annotation { "Feature Type Name" : "Feature", "Feature Type Description" : "" }
export const myFeature = defineFeature(function(context is Context, id is Id, definition is map)
    precondition{}
    {
        {
            var Q0;
            Q0=qCreatedBy(makeId("Right.planeOp"),FACE);
            var sketch = newSketch(context, id + "F0", { "sketchPlane" : qUnion([Q0])});
            skLineSegment(sketch, "E0", {"start": v(-15.9, -11.43) * mm, "end": v(-15.9, -19.05) * mm});
            skLineSegment(sketch, "E1", {"start": v(-15.9, -19.05) * mm, "end": v(-23.53, -19.05) * mm});
            skLineSegment(sketch, "E2", {"start": v(-23.53, 25.4) * mm, "end": v(-15.9, 25.4) * mm});
            skLineSegment(sketch, "E3", {"start": v(-15.9, 25.4) * mm, "end": v(0, 0) * mm});
            skLineSegment(sketch, "E4", {"start": v(0, 0) * mm, "end": v(0, 25.4) * mm});
            skLineSegment(sketch, "E5", {"start": v(0, 25.4) * mm, "end": v(7.62, 25.4) * mm});
            skLineSegment(sketch, "E6", {"start": v(7.62, 25.4) * mm, "end": v(7.62, -11.43) * mm});
            skLineSegment(sketch, "E7", {"start": v(-15.9, -11.43) * mm, "end": v(-15.9, 13.97) * mm});
            skLineSegment(sketch, "E8", {"start": v(-15.9, 13.97) * mm, "end": v(0, -11.43) * mm});
            skLineSegment(sketch, "E9", {"start": v(-15.9, -11.43) * mm, "end": v(0, -11.43) * mm});
            skLineSegment(sketch, "E10", {"start": v(0, -11.43) * mm, "end": v(7.62, -11.43) * mm});
            skLineSegment(sketch, "E11", {"start": v(0, -11.43) * mm, "end": v(0, -26.67) * mm});
            skLineSegment(sketch, "E12", {"start": v(0, -26.67) * mm, "end": v(7.62, -26.67) * mm});
            skLineSegment(sketch, "E13", {"start": v(7.62, -11.43) * mm, "end": v(7.62, -26.67) * mm});
            skLineSegment(sketch, "E14", {"start": v(-23.53, -19.05) * mm, "end": v(-23.53, 25.4) * mm});
            skSolve(sketch);
        }
        {
            var Q0;
            Q0=makeQuery(id+"F0.imprint","IMPRINT",FACE,{"disambiguationData":[TD([[makeQuery(id+"F0.imprint","IMPRINT",EDGE,{"derivedFrom":sQuery(id+"F0.wireOp",EDGE,"E0")}),-1.0]])]});
            extrude(context, id + "F1", {"entities" : qUnion([Q0]), "depth" : 127 * mm, "offsetDistance" : 25.4 * mm});
        }
        {
            var Q0;
            Q0=makeQuery(id+"F0.imprint","IMPRINT",FACE,{"disambiguationData":[TD([[makeQuery(id+"F0.imprint","IMPRINT",EDGE,{"derivedFrom":sQuery(id+"F0.wireOp",EDGE,"E10")}),-1.0]])]});
            extrude(context, id + "F2", {"entities" : qUnion([Q0]), "operationType" : NewBodyOperationType.ADD, "depth" : 127 * mm, "offsetDistance" : 25.4 * mm});
        }
        {
            var Q0;
            Q0=makeQuery(id+"F1.opExtrude","SWEPT_FACE",FACE,{"disambiguationData":[OSD([sQuery(id+"F0.wireOp",EDGE,"E14")])]});
            var sketch = newSketch(context, id + "F3", { "sketchPlane" : qUnion([Q0])});
            skLineSegment(sketch, "E15", {"start": v(0, 3.18) * mm, "end": v(0, 13.52) * mm});
            skText(sketch, "E16", { "text": "Nate Kolbeck\nCo-Founder 3DBK", "fontName": "AllertaStencil-Regular.ttf"});
            skLineSegment(sketch, "E17", {"start": v(127, 13.52) * mm, "end": v(100.83, 13.52) * mm});
            skLineSegment(sketch, "E18", {"start": v(113.91, 13.52) * mm, "end": v(109.05, 13.52) * mm});
            const initialGuessF3  = {"E16": [0, 0.00318, 1, 0, 0.01035]};
            skSetInitialGuess(sketch, initialGuessF3);
            skSolve(sketch);
        }
        {
            var Q0;
            {var subQ0=sQuery(id+"F3.wireOp",EDGE,"E15");Q0=makeQuery(id+"F3.imprint","IMPRINT",FACE,{"disambiguationData":[TD([[makeQuery(id+"F3.imprint","IMPRINT",EDGE,{"derivedFrom":subQ0}),-1.0]])]});}
            var sketch = newSketch(context, id + "F4", { "sketchPlane" : qUnion([Q0])});
            skLineSegment(sketch, "E19", {"start": v(114.47, 13.68) * mm, "end": v(109.84, 22.72) * mm});
            skLineSegment(sketch, "E20", {"start": v(109.84, 22.72) * mm, "end": v(103.5, 22.72) * mm});
            skLineSegment(sketch, "E21", {"start": v(103.5, 22.72) * mm, "end": v(108.12, 13.68) * mm});
            skLineSegment(sketch, "E22", {"start": v(108.12, 13.68) * mm, "end": v(114.47, 13.68) * mm});
            skLineSegment(sketch, "E23", {"start": v(103.5, 22.72) * mm, "end": v(106.67, 22.72) * mm});
            skLineSegment(sketch, "E24", {"start": v(106.67, 22.72) * mm, "end": v(105.08, 22.72) * mm});
            skLineSegment(sketch, "E25", {"start": v(106.67, 22.72) * mm, "end": v(109.84, 22.72) * mm});
            skLineSegment(sketch, "E26", {"start": v(108.25, 22.72) * mm, "end": v(109.84, 22.72) * mm});
            skLineSegment(sketch, "E27", {"start": v(109.84, 22.72) * mm, "end": v(112.15, 18.2) * mm});
            skLineSegment(sketch, "E28", {"start": v(112.15, 18.2) * mm, "end": v(111, 20.46) * mm});
            skLineSegment(sketch, "E29", {"start": v(111, 20.46) * mm, "end": v(109.84, 22.72) * mm});
            skLineSegment(sketch, "E30", {"start": v(108.12, 13.68) * mm, "end": v(107.54, 14.81) * mm});
            skLineSegment(sketch, "E31", {"start": v(112.15, 18.2) * mm, "end": v(105.8, 18.2) * mm});
            skLineSegment(sketch, "E32", {"start": v(109.7, 13.68) * mm, "end": v(111.3, 13.68) * mm});
            skLineSegment(sketch, "E33", {"start": v(108.25, 22.72) * mm, "end": v(109.05, 22.72) * mm});
            skLineSegment(sketch, "E34", {"start": v(112.88, 13.68) * mm, "end": v(114.47, 13.68) * mm});
            skLineSegment(sketch, "E35", {"start": v(113.68, 13.68) * mm, "end": v(114.47, 13.68) * mm});
            skLineSegment(sketch, "E36", {"start": v(103.5, 22.72) * mm, "end": v(105.08, 22.72) * mm});
            skLineSegment(sketch, "E37", {"start": v(104.28, 22.72) * mm, "end": v(105.08, 22.72) * mm});
            skLineSegment(sketch, "E38", {"start": v(108.12, 13.68) * mm, "end": v(109.7, 13.68) * mm});
            skLineSegment(sketch, "E39", {"start": v(108.91, 13.68) * mm, "end": v(109.7, 13.68) * mm});
            skLineSegment(sketch, "E40", {"start": v(108.12, 13.68) * mm, "end": v(108, 13.9) * mm});
            skEllipticalArc(sketch, "E41", {});
            skLineSegment(sketch, "E42", {"start": v(103.5, 22.72) * mm, "end": v(103.6, 22.5) * mm});
            skEllipticalArc(sketch, "E43", {});
            skPoint(sketch, "E44.endSnap0", {"position": v(113.56, 13.9) * mm});
            skEllipticalArc(sketch, "E45", {});
            skEllipticalArc(sketch, "E46", {});
            skLineSegment(sketch, "E47", {"start": v(109.06, 21.6) * mm, "end": v(112.53, 14.81) * mm});
            skLineSegment(sketch, "E48", {"start": v(110.2, 21.6) * mm, "end": v(113.66, 14.81) * mm});
            skEllipticalArc(sketch, "E49", {});
            skPoint(sketch, "E50.endSnap0", {"position": v(109.85, 16.5) * mm});
            skPoint(sketch, "E51.startSnap0", {"position": v(108.11, 19.9) * mm});
            skEllipticalArc(sketch, "E52", {});
            skLineSegment(sketch, "E53", {"start": v(106.35, 21.6) * mm, "end": v(109.35, 14.81) * mm});
            skLineSegment(sketch, "E54", {"start": v(111.68, 14.81) * mm, "end": v(108.48, 21.6) * mm});
            skLineSegment(sketch, "E55", {"start": v(104.25, 21.6) * mm, "end": v(107.71, 14.81) * mm});
            skLineSegment(sketch, "E56", {"start": v(108.95, 14.81) * mm, "end": v(105.47, 21.6) * mm});
            const initialGuessF4  = {"E41": [0.10833149728310405, 0.014810047057404773, 0.4554737955281724, -0.8902491907253614, 0.00101929742591525, 0.0005757361731481606, 4.431068627539217, 1.2894759739518464], "E43": [0.10486257227566997, 0.021590256392991263, -0.4554737955281669, 0.8902491907253641, 0.0010134030675351836, 0.0005632368300749493, 4.435346609303014, 1.2937539557132312], "E45": [0.10962539112028638, 0.021590256392991267, -0.4556727507455257, 0.8901473721963157, 0.0010135189845315016, 0.0005231169472103337, 4.454076555073977, 1.312483901484343], "E46": [0.113096228349131, 0.014810047057404768, 0.45567275074552593, -0.8901473721963156, 0.001019414017131275, 0.0005212198721764481, 4.456396634300917, 1.3148039807094034], "E49": [0.1102215076819885, 0.015772615629219357, 0.45559915121396044, -0.8901850444784606, 0.0021006837757420087, 0.0012411979836777346, 4.933929888195674, 0.7619395356004123], "E52": [0.10774158553112072, 0.020618080341546333, -0.45559915121395933, 0.8901850444784613, 0.002105581669589703, 0.0011367591904601947, 4.9663310785315185, 0.777684001741559]};
            skSetInitialGuess(sketch, initialGuessF4);
            skSolve(sketch);
        }
        {
            var Q0;
            {var subQ5=sQuery(id+"F4.wireOp",EDGE,"E43");Q0=makeQuery(id+"F4.imprint","IMPRINT",FACE,{"disambiguationData":[TD([[makeQuery(id+"F4.imprint","IMPRINT",EDGE,{"derivedFrom":subQ5}),1.0]])]});}
            var Q1;
            {var subQ5=sQuery(id+"F4.wireOp",EDGE,"E52");Q1=makeQuery(id+"F4.imprint","IMPRINT",FACE,{"disambiguationData":[TD([[makeQuery(id+"F4.imprint","IMPRINT",EDGE,{"derivedFrom":subQ5}),1.0]])]});}
            var Q2;
            {var subQ5=sQuery(id+"F4.wireOp",EDGE,"E41");Q2=makeQuery(id+"F4.imprint","IMPRINT",FACE,{"disambiguationData":[TD([[makeQuery(id+"F4.imprint","IMPRINT",EDGE,{"derivedFrom":subQ5}),1.0]])]});}
            var Q3;
            {var subQ5=sQuery(id+"F4.wireOp",EDGE,"E49");Q3=makeQuery(id+"F4.imprint","IMPRINT",FACE,{"disambiguationData":[TD([[makeQuery(id+"F4.imprint","IMPRINT",EDGE,{"derivedFrom":subQ5}),1.0]])]});}
            var Q4;
            {var subQ5=sQuery(id+"F4.wireOp",EDGE,"E45");Q4=makeQuery(id+"F4.imprint","IMPRINT",FACE,{"disambiguationData":[TD([[makeQuery(id+"F4.imprint","IMPRINT",EDGE,{"derivedFrom":subQ5}),1.0]])]});}
            var Q5;
            {var subQ5=sQuery(id+"F4.wireOp",EDGE,"E46");Q5=makeQuery(id+"F4.imprint","IMPRINT",FACE,{"disambiguationData":[TD([[makeQuery(id+"F4.imprint","IMPRINT",EDGE,{"derivedFrom":subQ5}),1.0]])]});}
            extrude(context, id + "F5", {"entities" : qUnion([Q0, Q1, Q2, Q3, Q4, Q5]), "operationType" : NewBodyOperationType.REMOVE, "oppositeDirection" : true, "depth" : 2.54 * mm, "offsetDistance" : 25.4 * mm});
        }
        {
            var Q0;
            {var subQ1=sQuery(id+"F4.wireOp",EDGE,"E43");Q0=makeQuery(id+"F4.imprint","IMPRINT",FACE,{"disambiguationData":[TD([[makeQuery(id+"F4.imprint","IMPRINT",EDGE,{"derivedFrom":subQ1}),-1.0]])]});}
            var Q1;
            {var subQ5=sQuery(id+"F4.wireOp",EDGE,"E41");Q1=makeQuery(id+"F4.imprint","IMPRINT",FACE,{"disambiguationData":[TD([[makeQuery(id+"F4.imprint","IMPRINT",EDGE,{"derivedFrom":subQ5}),-1.0]])]});}
            extrude(context, id + "F6", {"entities" : qUnion([Q0, Q1]), "operationType" : NewBodyOperationType.ADD, "depth" : 0.5 * mm, "offsetDistance" : 25.4 * mm});
        }
        {
            var Q0;
            Q0=makeQuery(id+"F6.opExtrude","CAP_EDGE",EDGE,{"disambiguationData":[OSD([sQuery(id+"F4.wireOp",EDGE,"E19")])],"isStart":false});
            fillet(context, id + "F7", {"entities" : qUnion([Q0]), "radius" : 5.08 * mm, "tangentPropagation" : true, "allowEdgeOverflow" : false});
        }
        {
            var Q0;
            Q0=makeQuery(id+"F6.opExtrude","CAP_EDGE",EDGE,{"disambiguationData":[OSD([sQuery(id+"F4.wireOp",EDGE,"E21")])],"isStart":false});
            fillet(context, id + "F8", {"entities" : qUnion([Q0]), "radius" : 5.08 * mm, "tangentPropagation" : true, "allowEdgeOverflow" : false});
        }
        {
            var Q0;
            {Q0=qUnion([makeQuery(id+"F3.imprint","IMPRINT",FACE,{"disambiguationData":[TD([[makeQuery(id+"F3.imprint","IMPRINT",EDGE,{"derivedFrom":sQuery(id+"F3.wireOp",EDGE,"E16.sketch_text.stroke-0")}),-1.0]])]}),makeQuery(id+"F3.imprint","IMPRINT",FACE,{"disambiguationData":[TD([[makeQuery(id+"F3.imprint","IMPRINT",EDGE,{"derivedFrom":sQuery(id+"F3.wireOp",EDGE,"E16.sketch_text.stroke-7")}),-1.0]])]}),makeQuery(id+"F3.imprint","IMPRINT",FACE,{"disambiguationData":[TD([[makeQuery(id+"F3.imprint","IMPRINT",EDGE,{"derivedFrom":sQuery(id+"F3.wireOp",EDGE,"E16.sketch_text.stroke-11")}),-1.0]])]}),makeQuery(id+"F3.imprint","IMPRINT",FACE,{"disambiguationData":[TD([[makeQuery(id+"F3.imprint","IMPRINT",EDGE,{"derivedFrom":sQuery(id+"F3.wireOp",EDGE,"E16.sketch_text.stroke-30")}),-1.0]])]}),makeQuery(id+"F3.imprint","IMPRINT",FACE,{"disambiguationData":[TD([[makeQuery(id+"F3.imprint","IMPRINT",EDGE,{"derivedFrom":sQuery(id+"F3.wireOp",EDGE,"E16.sketch_text.stroke-66")}),-1.0]])]}),makeQuery(id+"F3.imprint","IMPRINT",FACE,{"disambiguationData":[TD([[makeQuery(id+"F3.imprint","IMPRINT",EDGE,{"derivedFrom":sQuery(id+"F3.wireOp",EDGE,"E16.sketch_text.stroke-91")}),-1.0]])]}),makeQuery(id+"F3.imprint","IMPRINT",FACE,{"disambiguationData":[TD([[makeQuery(id+"F3.imprint","IMPRINT",EDGE,{"derivedFrom":sQuery(id+"F3.wireOp",EDGE,"E16.sketch_text.stroke-104")}),-1.0]])]}),makeQuery(id+"F3.imprint","IMPRINT",FACE,{"disambiguationData":[TD([[makeQuery(id+"F3.imprint","IMPRINT",EDGE,{"derivedFrom":sQuery(id+"F3.wireOp",EDGE,"E16.sketch_text.stroke-128")}),-1.0]])]}),makeQuery(id+"F3.imprint","IMPRINT",FACE,{"disambiguationData":[TD([[makeQuery(id+"F3.imprint","IMPRINT",EDGE,{"derivedFrom":sQuery(id+"F3.wireOp",EDGE,"E16.sketch_text.stroke-132")}),-1.0]])]}),makeQuery(id+"F3.imprint","IMPRINT",FACE,{"disambiguationData":[TD([[makeQuery(id+"F3.imprint","IMPRINT",EDGE,{"derivedFrom":sQuery(id+"F3.wireOp",EDGE,"E16.sketch_text.stroke-139")}),-1.0]])]}),makeQuery(id+"F3.imprint","IMPRINT",FACE,{"disambiguationData":[TD([[makeQuery(id+"F3.imprint","IMPRINT",EDGE,{"derivedFrom":sQuery(id+"F3.wireOp",EDGE,"E16.sketch_text.stroke-155")}),-1.0]])]}),makeQuery(id+"F3.imprint","IMPRINT",FACE,{"disambiguationData":[TD([[makeQuery(id+"F3.imprint","IMPRINT",EDGE,{"derivedFrom":sQuery(id+"F3.wireOp",EDGE,"E16.sketch_text.stroke-171")}),-1.0]])]}),makeQuery(id+"F3.imprint","IMPRINT",FACE,{"disambiguationData":[TD([[makeQuery(id+"F3.imprint","IMPRINT",EDGE,{"derivedFrom":sQuery(id+"F3.wireOp",EDGE,"E16.sketch_text.stroke-189")}),-1.0]])]}),makeQuery(id+"F3.imprint","IMPRINT",FACE,{"disambiguationData":[TD([[makeQuery(id+"F3.imprint","IMPRINT",EDGE,{"derivedFrom":sQuery(id+"F3.wireOp",EDGE,"E16.sketch_text.stroke-195")}),-1.0]])]}),makeQuery(id+"F3.imprint","IMPRINT",FACE,{"disambiguationData":[TD([[makeQuery(id+"F3.imprint","IMPRINT",EDGE,{"derivedFrom":sQuery(id+"F3.wireOp",EDGE,"E16.sketch_text.stroke-222")}),-1.0]])]}),makeQuery(id+"F3.imprint","IMPRINT",FACE,{"disambiguationData":[TD([[makeQuery(id+"F3.imprint","IMPRINT",EDGE,{"derivedFrom":sQuery(id+"F3.wireOp",EDGE,"E16.sketch_text.stroke-235")}),-1.0]])]}),makeQuery(id+"F3.imprint","IMPRINT",FACE,{"disambiguationData":[TD([[makeQuery(id+"F3.imprint","IMPRINT",EDGE,{"derivedFrom":sQuery(id+"F3.wireOp",EDGE,"E16.sketch_text.stroke-259")}),-1.0]])]}),makeQuery(id+"F3.imprint","IMPRINT",FACE,{"disambiguationData":[TD([[makeQuery(id+"F3.imprint","IMPRINT",EDGE,{"derivedFrom":sQuery(id+"F3.wireOp",EDGE,"E16.sketch_text.stroke-265")}),-1.0]])]}),makeQuery(id+"F3.imprint","IMPRINT",FACE,{"disambiguationData":[TD([[makeQuery(id+"F3.imprint","IMPRINT",EDGE,{"derivedFrom":sQuery(id+"F3.wireOp",EDGE,"E16.sketch_text.stroke-271")}),-1.0]])]}),makeQuery(id+"F3.imprint","IMPRINT",FACE,{"disambiguationData":[TD([[makeQuery(id+"F3.imprint","IMPRINT",EDGE,{"derivedFrom":sQuery(id+"F3.wireOp",EDGE,"E16.sketch_text.stroke-287")}),-1.0]])]}),makeQuery(id+"F3.imprint","IMPRINT",FACE,{"disambiguationData":[TD([[makeQuery(id+"F3.imprint","IMPRINT",EDGE,{"derivedFrom":sQuery(id+"F3.wireOp",EDGE,"E16.sketch_text.stroke-294")}),-1.0]])]}),makeQuery(id+"F3.imprint","IMPRINT",FACE,{"disambiguationData":[TD([[makeQuery(id+"F3.imprint","IMPRINT",EDGE,{"derivedFrom":sQuery(id+"F3.wireOp",EDGE,"E16.sketch_text.stroke-298")}),-1.0]])]}),makeQuery(id+"F3.imprint","IMPRINT",FACE,{"disambiguationData":[TD([[makeQuery(id+"F3.imprint","IMPRINT",EDGE,{"derivedFrom":sQuery(id+"F3.wireOp",EDGE,"E16.sketch_text.stroke-303")}),-1.0]])]}),makeQuery(id+"F3.imprint","IMPRINT",FACE,{"disambiguationData":[TD([[makeQuery(id+"F3.imprint","IMPRINT",EDGE,{"derivedFrom":sQuery(id+"F3.wireOp",EDGE,"E16.sketch_text.stroke-309")}),-1.0]])]}),makeQuery(id+"F3.imprint","IMPRINT",FACE,{"disambiguationData":[TD([[makeQuery(id+"F3.imprint","IMPRINT",EDGE,{"derivedFrom":sQuery(id+"F3.wireOp",EDGE,"E16.sketch_text.stroke-327")}),-1.0]])]}),makeQuery(id+"F3.imprint","IMPRINT",FACE,{"disambiguationData":[TD([[makeQuery(id+"F3.imprint","IMPRINT",EDGE,{"derivedFrom":sQuery(id+"F3.wireOp",EDGE,"E16.sketch_text.stroke-343")}),-1.0]])]}),makeQuery(id+"F3.imprint","IMPRINT",FACE,{"disambiguationData":[TD([[makeQuery(id+"F3.imprint","IMPRINT",EDGE,{"derivedFrom":sQuery(id+"F3.wireOp",EDGE,"E16.sketch_text.stroke-359")}),-1.0]])]}),makeQuery(id+"F3.imprint","IMPRINT",FACE,{"disambiguationData":[TD([[makeQuery(id+"F3.imprint","IMPRINT",EDGE,{"derivedFrom":sQuery(id+"F3.wireOp",EDGE,"E16.sketch_text.stroke-363")}),-1.0]])]}),makeQuery(id+"F3.imprint","IMPRINT",FACE,{"disambiguationData":[TD([[makeQuery(id+"F3.imprint","IMPRINT",EDGE,{"derivedFrom":sQuery(id+"F3.wireOp",EDGE,"E16.sketch_text.stroke-367")}),-1.0]])]}),makeQuery(id+"F3.imprint","IMPRINT",FACE,{"disambiguationData":[TD([[makeQuery(id+"F3.imprint","IMPRINT",EDGE,{"derivedFrom":sQuery(id+"F3.wireOp",EDGE,"E16.sketch_text.stroke-371")}),-1.0]])]}),makeQuery(id+"F3.imprint","IMPRINT",FACE,{"disambiguationData":[TD([[makeQuery(id+"F3.imprint","IMPRINT",EDGE,{"derivedFrom":sQuery(id+"F3.wireOp",EDGE,"E16.sketch_text.stroke-375")}),-1.0]])]}),makeQuery(id+"F3.imprint","IMPRINT",FACE,{"disambiguationData":[TD([[makeQuery(id+"F3.imprint","IMPRINT",EDGE,{"derivedFrom":sQuery(id+"F3.wireOp",EDGE,"E16.sketch_text.stroke-391")}),-1.0]])]}),makeQuery(id+"F3.imprint","IMPRINT",FACE,{"disambiguationData":[TD([[makeQuery(id+"F3.imprint","IMPRINT",EDGE,{"derivedFrom":sQuery(id+"F3.wireOp",EDGE,"E16.sketch_text.stroke-407")}),-1.0]])]}),makeQuery(id+"F3.imprint","IMPRINT",FACE,{"disambiguationData":[TD([[makeQuery(id+"F3.imprint","IMPRINT",EDGE,{"derivedFrom":sQuery(id+"F3.wireOp",EDGE,"E16.sketch_text.stroke-427")}),-1.0]])]}),makeQuery(id+"F3.imprint","IMPRINT",FACE,{"disambiguationData":[TD([[makeQuery(id+"F3.imprint","IMPRINT",EDGE,{"derivedFrom":sQuery(id+"F3.wireOp",EDGE,"E16.sketch_text.stroke-432")}),-1.0]])]}),makeQuery(id+"F3.imprint","IMPRINT",FACE,{"disambiguationData":[TD([[makeQuery(id+"F3.imprint","IMPRINT",EDGE,{"derivedFrom":sQuery(id+"F3.wireOp",EDGE,"E16.sketch_text.stroke-437")}),-1.0]])]}),makeQuery(id+"F3.imprint","IMPRINT",FACE,{"disambiguationData":[TD([[makeQuery(id+"F3.imprint","IMPRINT",EDGE,{"derivedFrom":sQuery(id+"F3.wireOp",EDGE,"E16.sketch_text.stroke-456")}),-1.0]])]}),makeQuery(id+"F3.imprint","IMPRINT",FACE,{"disambiguationData":[TD([[makeQuery(id+"F3.imprint","IMPRINT",EDGE,{"derivedFrom":sQuery(id+"F3.wireOp",EDGE,"E16.sketch_text.stroke-461")}),-1.0]])]}),makeQuery(id+"F3.imprint","IMPRINT",FACE,{"disambiguationData":[TD([[makeQuery(id+"F3.imprint","IMPRINT",EDGE,{"derivedFrom":sQuery(id+"F3.wireOp",EDGE,"E16.sketch_text.stroke-486")}),-1.0]])]}),makeQuery(id+"F3.imprint","IMPRINT",FACE,{"disambiguationData":[TD([[makeQuery(id+"F3.imprint","IMPRINT",EDGE,{"derivedFrom":sQuery(id+"F3.wireOp",EDGE,"E16.sketch_text.stroke-499")}),-1.0]])]}),makeQuery(id+"F3.imprint","IMPRINT",FACE,{"disambiguationData":[TD([[makeQuery(id+"F3.imprint","IMPRINT",EDGE,{"derivedFrom":sQuery(id+"F3.wireOp",EDGE,"E16.sketch_text.stroke-523")}),-1.0]])]}),makeQuery(id+"F3.imprint","IMPRINT",FACE,{"disambiguationData":[TD([[makeQuery(id+"F3.imprint","IMPRINT",EDGE,{"derivedFrom":sQuery(id+"F3.wireOp",EDGE,"E16.sketch_text.stroke-530")}),-1.0]])]}),makeQuery(id+"F3.imprint","IMPRINT",FACE,{"disambiguationData":[TD([[makeQuery(id+"F3.imprint","IMPRINT",EDGE,{"derivedFrom":sQuery(id+"F3.wireOp",EDGE,"E16.sketch_text.stroke-537")}),-1.0]])]}),makeQuery(id+"F3.imprint","IMPRINT",FACE,{"disambiguationData":[TD([[makeQuery(id+"F3.imprint","IMPRINT",EDGE,{"derivedFrom":sQuery(id+"F3.wireOp",EDGE,"E16.sketch_text.stroke-583")}),-1.0]])]}),makeQuery(id+"F3.imprint","IMPRINT",FACE,{"disambiguationData":[TD([[makeQuery(id+"F3.imprint","IMPRINT",EDGE,{"derivedFrom":sQuery(id+"F3.wireOp",EDGE,"E16.sketch_text.stroke-587")}),-1.0]])]}),makeQuery(id+"F3.imprint","IMPRINT",FACE,{"disambiguationData":[TD([[makeQuery(id+"F3.imprint","IMPRINT",EDGE,{"derivedFrom":sQuery(id+"F3.wireOp",EDGE,"E16.sketch_text.stroke-609")}),-1.0]])]}),makeQuery(id+"F3.imprint","IMPRINT",FACE,{"disambiguationData":[TD([[makeQuery(id+"F3.imprint","IMPRINT",EDGE,{"derivedFrom":sQuery(id+"F3.wireOp",EDGE,"E16.sketch_text.stroke-648")}),-1.0]])]}),makeQuery(id+"F3.imprint","IMPRINT",FACE,{"disambiguationData":[TD([[makeQuery(id+"F3.imprint","IMPRINT",EDGE,{"derivedFrom":sQuery(id+"F3.wireOp",EDGE,"E16.sketch_text.stroke-652")}),-1.0]])]}),makeQuery(id+"F3.imprint","IMPRINT",FACE,{"disambiguationData":[TD([[makeQuery(id+"F3.imprint","IMPRINT",EDGE,{"derivedFrom":sQuery(id+"F3.wireOp",EDGE,"E16.sketch_text.stroke-656")}),-1.0]])]})]);}
            extrude(context, id + "F9", {"entities" : qUnion([Q0]), "operationType" : NewBodyOperationType.REMOVE, "oppositeDirection" : true, "depth" : 2.54 * mm, "offsetDistance" : 25.4 * mm});
        }
    });